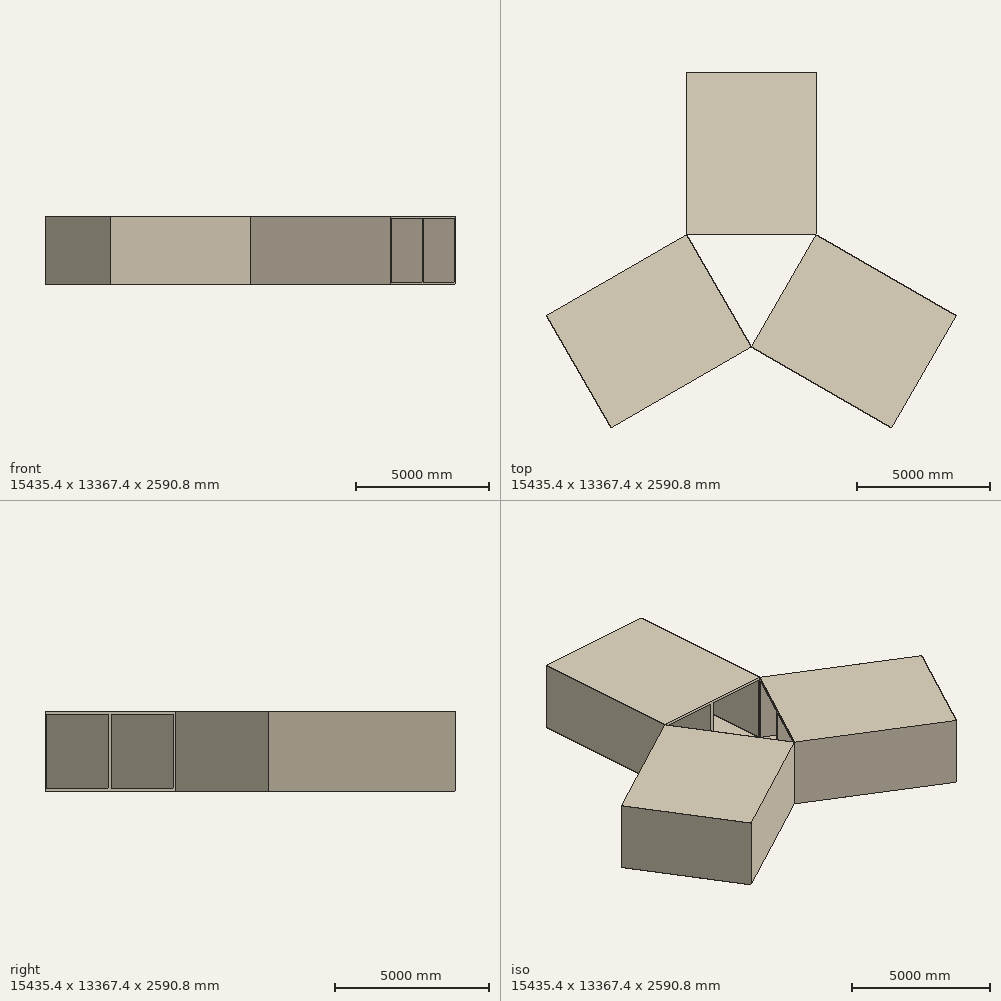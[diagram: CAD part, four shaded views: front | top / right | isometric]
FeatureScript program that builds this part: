
annotation { "Feature Type Name" : "Feature", "Feature Type Description" : "" }
export const myFeature = defineFeature(function(context is Context, id is Id, definition is map)
    precondition{}
    {
        {
            var Q0;
            Q0=qCreatedBy(makeId("Top.planeOp"),FACE);
            var sketch = newSketch(context, id + "F0", { "sketchPlane" : qUnion([Q0])});
            skLineSegment(sketch, "E0.bottom", {"start": v(-2438.4, 3048) * mm, "end": v(2438.4, 3048) * mm});
            skLineSegment(sketch, "E0.top", {"start": v(-2438.4, -3048) * mm, "end": v(2438.4, -3048) * mm});
            skLineSegment(sketch, "E0.left", {"start": v(-2438.4, 3048) * mm, "end": v(-2438.4, -3048) * mm});
            skLineSegment(sketch, "E0.right", {"start": v(2438.4, 3048) * mm, "end": v(2438.4, -3048) * mm});
            skPoint(sketch, "E0.middle", {"position": v(0, 0) * mm});
            skLineSegment(sketch, "E1", {"start": v(0, 3048) * mm, "end": v(0, -3048) * mm, "construction": true});
            skLineSegment(sketch, "E2", {"start": v(-2438.4, -3048) * mm, "end": v(-7717.7, -6096) * mm});
            skLineSegment(sketch, "E3", {"start": v(-7717.7, -6096) * mm, "end": v(-5279.3, -10319.43) * mm});
            skLineSegment(sketch, "E4", {"start": v(-5279.3, -10319.43) * mm, "end": v(0, -7271.43) * mm});
            skLineSegment(sketch, "E5", {"start": v(0, -7271.43) * mm, "end": v(-2438.4, -3048) * mm});
            skLineSegment(sketch, "E6.MirrorCS", {"start": v(2438.4, -3048) * mm, "end": v(7717.7, -6096) * mm});
            skLineSegment(sketch, "E7.MirrorCS", {"start": v(0, -7271.43) * mm, "end": v(2438.4, -3048) * mm});
            skLineSegment(sketch, "E8.MirrorCS", {"start": v(5279.3, -10319.43) * mm, "end": v(0, -7271.43) * mm});
            skLineSegment(sketch, "E9.MirrorCS", {"start": v(7717.7, -6096) * mm, "end": v(5279.3, -10319.43) * mm});
            skLineSegment(sketch, "E10", {"start": v(0, 0) * mm, "end": v(8805.15, 0) * mm, "construction": true});
            skLineSegment(sketch, "E11.MirrorCS", {"start": v(-2438.4, 3048) * mm, "end": v(-7717.7, 6096) * mm});
            skLineSegment(sketch, "E12.MirrorCS", {"start": v(0, 7271.43) * mm, "end": v(-2438.4, 3048) * mm});
            skLineSegment(sketch, "E13.MirrorCS", {"start": v(-5279.3, 10319.43) * mm, "end": v(0, 7271.43) * mm});
            skLineSegment(sketch, "E14.MirrorCS", {"start": v(-7717.7, 6096) * mm, "end": v(-5279.3, 10319.43) * mm});
            skLineSegment(sketch, "E15.MirrorCS", {"start": v(0, 7271.43) * mm, "end": v(2438.4, 3048) * mm});
            skLineSegment(sketch, "E16.MirrorCS", {"start": v(2438.4, 3048) * mm, "end": v(7717.7, 6096) * mm});
            skLineSegment(sketch, "E17.MirrorCS", {"start": v(5279.3, 10319.43) * mm, "end": v(0, 7271.43) * mm});
            skLineSegment(sketch, "E18.MirrorCS", {"start": v(7717.7, 6096) * mm, "end": v(5279.3, 10319.43) * mm});
            skSolve(sketch);
        }
        {
            var Q0;
            Q0=makeQuery(id+"F0.imprint","IMPRINT",FACE,{"disambiguationData":[TD([[makeQuery(id+"F0.imprint","IMPRINT",EDGE,{"derivedFrom":sQuery(id+"F0.wireOp",EDGE,"E2")}),1.0]])]});
            var Q1;
            Q1=makeQuery(id+"F0.imprint","IMPRINT",FACE,{"disambiguationData":[TD([[makeQuery(id+"F0.imprint","IMPRINT",EDGE,{"derivedFrom":sQuery(id+"F0.wireOp",EDGE,"E6.MirrorCS")}),-1.0]])]});
            extrude(context, id + "F1", {"entities" : qUnion([Q0, Q1]), "depth" : 2590.8 * mm, "offsetDistance" : 25.4 * mm});
        }
        {
            var Q0;
            Q0=makeQuery(id+"F0.imprint","IMPRINT",FACE,{"disambiguationData":[TD([[makeQuery(id+"F0.imprint","IMPRINT",EDGE,{"derivedFrom":sQuery(id+"F0.wireOp",EDGE,"E0.bottom")}),-1.0]])]});
            extrude(context, id + "F2", {"entities" : qUnion([Q0]), "depth" : 2590.8 * mm, "offsetDistance" : 25.4 * mm});
        }
        {
            var Q0;
            Q0=makeQuery(id+"F1.opExtrude","SWEPT_FACE",FACE,{"disambiguationData":[OSD([sQuery(id+"F0.wireOp",EDGE,"E9.MirrorCS")])]});
            var sketch = newSketch(context, id + "F3", { "sketchPlane" : qUnion([Q0])});
            skLineSegment(sketch, "E19.bottom", {"start": v(-6246.45, 2489.2) * mm, "end": v(-3909.65, 2489.2) * mm});
            skLineSegment(sketch, "E19.top", {"start": v(-6246.45, 101.6) * mm, "end": v(-3909.65, 101.6) * mm});
            skLineSegment(sketch, "E19.left", {"start": v(-6246.45, 2489.2) * mm, "end": v(-6246.45, 101.6) * mm});
            skLineSegment(sketch, "E19.right", {"start": v(-3909.65, 2489.2) * mm, "end": v(-3909.65, 101.6) * mm});
            skLineSegment(sketch, "E20", {"start": v(-3858.85, 2590.8) * mm, "end": v(-3858.85, 0) * mm, "construction": true});
            skLineSegment(sketch, "E21", {"start": v(-3858.85, 1295.4) * mm, "end": v(-3909.65, 1295.4) * mm, "construction": true});
            skLineSegment(sketch, "E22", {"start": v(-3858.85, 2590.8) * mm, "end": v(-6297.25, 2590.8) * mm, "construction": true});
            skLineSegment(sketch, "E23", {"start": v(-5078.05, 2489.2) * mm, "end": v(-5078.05, 2590.8) * mm, "construction": true});
            skLineSegment(sketch, "E24.MirrorCS", {"start": v(-1471.25, 2489.2) * mm, "end": v(-3808.05, 2489.2) * mm});
            skLineSegment(sketch, "E25.MirrorCS", {"start": v(-1471.25, 2489.2) * mm, "end": v(-1471.25, 101.6) * mm});
            skLineSegment(sketch, "E26.MirrorCS", {"start": v(-1471.25, 101.6) * mm, "end": v(-3808.05, 101.6) * mm});
            skLineSegment(sketch, "E27.MirrorCS", {"start": v(-3808.05, 2489.2) * mm, "end": v(-3808.05, 101.6) * mm});
            skSolve(sketch);
        }
        {
            var Q0;
            Q0 = qSketchRegion(id + "F3", true);
            extrude(context, id + "F4", {"entities" : qUnion([Q0]), "operationType" : NewBodyOperationType.REMOVE, "endBound" : BoundingType.UP_TO_NEXT, "oppositeDirection" : true, "depth" : 25.4 * mm, "offsetDistance" : 25.4 * mm});
        }
        {
            var Q0;
            Q0=makeQuery(id+"F2.opExtrude","SWEPT_FACE",FACE,{"disambiguationData":[OSD([sQuery(id+"F0.wireOp",EDGE,"E0.bottom")])]});
            var sketch = newSketch(context, id + "F5", { "sketchPlane" : qUnion([Q0])});
            skLineSegment(sketch, "E28.bottom", {"start": v(-2378.16, 2489.2) * mm, "end": v(-41.36, 2489.2) * mm});
            skLineSegment(sketch, "E28.top", {"start": v(-2378.16, 101.6) * mm, "end": v(-41.36, 101.6) * mm});
            skLineSegment(sketch, "E28.left", {"start": v(-2378.16, 2489.2) * mm, "end": v(-2378.16, 101.6) * mm});
            skLineSegment(sketch, "E28.right", {"start": v(-41.36, 2489.2) * mm, "end": v(-41.36, 101.6) * mm});
            skLineSegment(sketch, "E29", {"start": v(18.88, 2590.8) * mm, "end": v(18.88, 0) * mm, "construction": true});
            skLineSegment(sketch, "E30", {"start": v(18.88, 1295.4) * mm, "end": v(-41.36, 1295.4) * mm, "construction": true});
            skLineSegment(sketch, "E31", {"start": v(18.88, 2590.8) * mm, "end": v(-2438.4, 2590.8) * mm, "construction": true});
            skLineSegment(sketch, "E32", {"start": v(-1209.76, 2489.2) * mm, "end": v(-1209.76, 2590.8) * mm, "construction": true});
            skLineSegment(sketch, "E33.MirrorCS", {"start": v(2415.92, 2489.2) * mm, "end": v(79.12, 2489.2) * mm});
            skLineSegment(sketch, "E34.MirrorCS", {"start": v(2415.92, 2489.2) * mm, "end": v(2415.92, 101.6) * mm});
            skLineSegment(sketch, "E35.MirrorCS", {"start": v(2415.92, 101.6) * mm, "end": v(79.12, 101.6) * mm});
            skLineSegment(sketch, "E36.MirrorCS", {"start": v(79.12, 2489.2) * mm, "end": v(79.12, 101.6) * mm});
            skSolve(sketch);
        }
        {
            var Q0;
            Q0 = qSketchRegion(id + "F5", true);
            extrude(context, id + "F6", {"entities" : qUnion([Q0]), "operationType" : NewBodyOperationType.REMOVE, "endBound" : BoundingType.UP_TO_NEXT, "oppositeDirection" : true, "depth" : 25.4 * mm, "offsetDistance" : 25.4 * mm});
        }
    });
